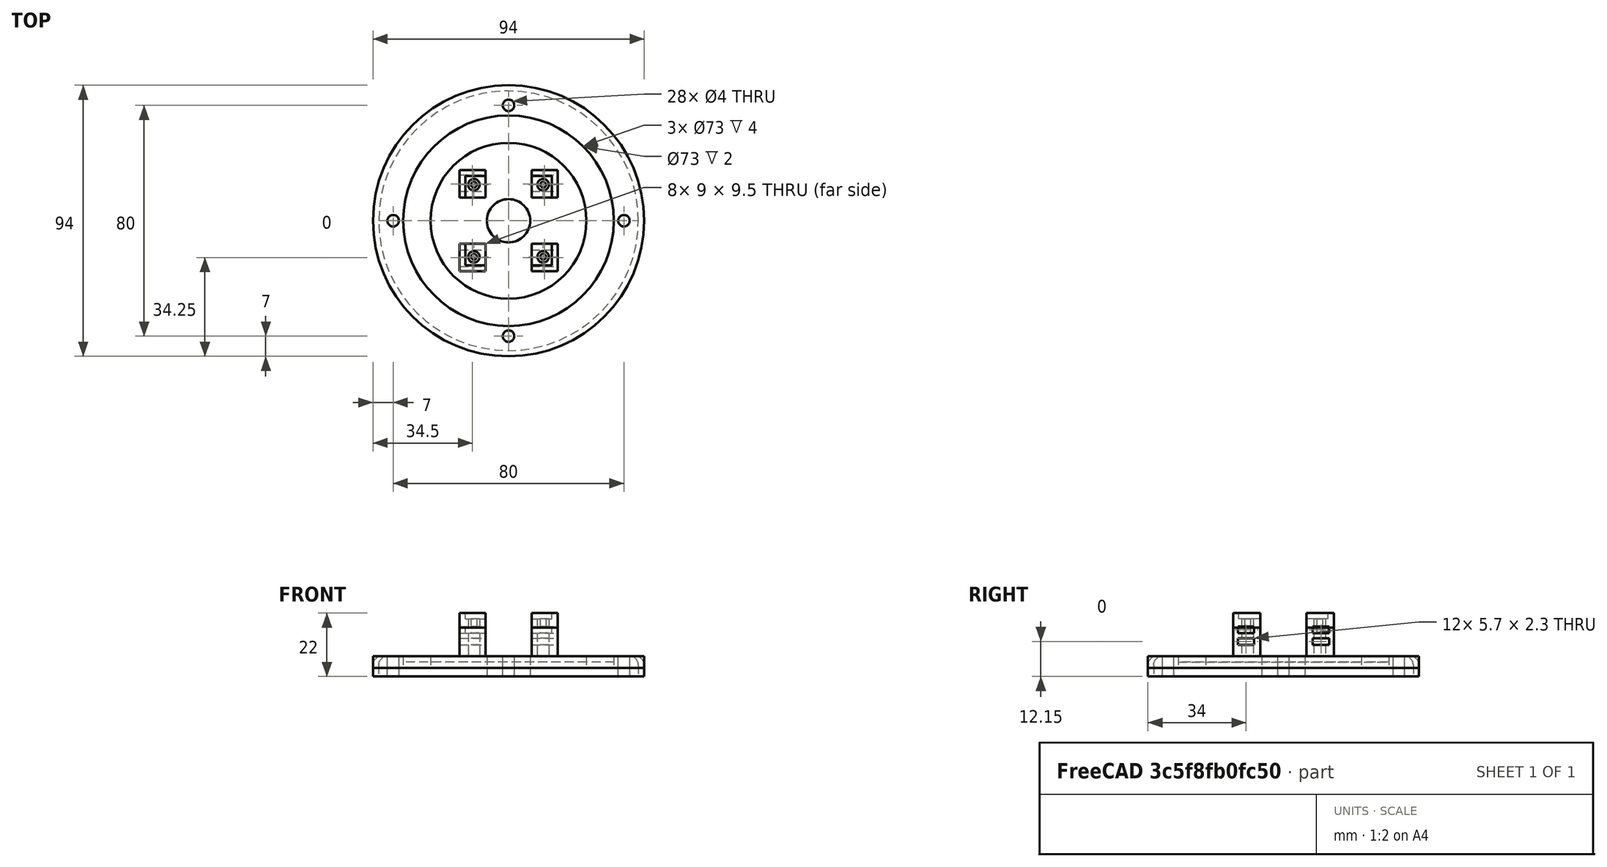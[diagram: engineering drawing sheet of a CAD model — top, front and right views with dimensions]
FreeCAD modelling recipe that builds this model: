
FCSTD DOCUMENT  (FreeCAD 0.16R6700 (Git))
Label: pieza7v1
License: CreativeCommons Attribution-ShareAlike
LicenseURL: http://creativecommons.org/licenses/by-sa/4.0/
objects: Part::Cut×26, Part::Cylinder×16, Part::Feature×12, Part::Box×10, Part::MultiFuse×3, Part::Fillet×2
note: 69 computed .brp shape members not serialized (recipe doc carries the construction recipe); baked Part::Feature solids carry a one-line shape summary decoded from their .brp

FEATURE [Part::Cylinder] Cylinder005  label="Cilindro004"
  Angle = 360
  Height = 5
  Radius = 36.5
FEATURE [Part::Cylinder] Cylinder006  label="Cilindro005"
  Angle = 360
  Height = 8
  Placement = pos=(0,0,-2) rot=(0,0,1;0rad)
  Radius = 27
FEATURE [Part::Cut] Cut016002
  Base = -> Cylinder005
  Placement = pos=(0,0,55) rot=(0,0,1;0rad)
  Tool = -> Cylinder006
FEATURE [Part::Cylinder] Cylinder007  label="prePortaLamH001"
  Angle = 360
  Height = 7
  Placement = pos=(0,0,56) rot=(0,0,1;0rad)
  Radius = 47
FEATURE [Part::Feature] Clone020  label=" taladroTuercaM030"
  Placement = pos=(-1e-11,30,75.05) rot=(1,0,0;3.14159rad)
  shape: bbox 6.7 x 5.802 x 32.25 mm, 10 faces (baked)
FEATURE [Part::Feature] Clone021  label=" taladroTuercaM031"
  Placement = pos=(40,-10,75.05) rot=(1,0,0;3.14159rad)
  shape: bbox 6.7 x 5.802 x 32.25 mm, 10 faces (baked)
FEATURE [Part::Feature] Clone022  label=" taladroTuercaM032"
  Placement = pos=(-1e-11,-50,75.05) rot=(1,0,0;3.14159rad)
  shape: bbox 6.7 x 5.802 x 32.25 mm, 10 faces (baked)
FEATURE [Part::Feature] Clone023  label=" taladroTuercaM033"
  Placement = pos=(-40,-10,75.05) rot=(1,0,0;3.14159rad)
  shape: bbox 6.7 x 5.802 x 32.25 mm, 10 faces (baked)
FEATURE [Part::Cut] Cut016015
  Base = -> Cylinder007
  Tool = -> Cut016002
FEATURE [Part::Cut] Cut016016
  Base = -> Cut016015
  Tool = -> Clone020
FEATURE [Part::Cut] Cut016017
  Base = -> Cut016016
  Tool = -> Clone021
FEATURE [Part::Cut] Cut016018
  Base = -> Cut016017
  Tool = -> Clone022
FEATURE [Part::Cut] Cut016019  label="prePortaCamV2"
  Base = -> Cut016018
  Tool = -> Clone023
FEATURE [Part::Cylinder] Cylinder008  label="Cilindro006"
  Angle = 360
  Height = 25
  Placement = pos=(0,0,43) rot=(0,0,1;0rad)
  Radius = 7.5
FEATURE [Part::Cut] Cut016020
  Base = -> Cut016019
  Tool = -> Cylinder008
FEATURE [Part::Box] Box015  label="Cubo015"
  Height = 2
  Length = 30
  Placement = pos=(-15,-15.5,41) rot=(0,0,1;0rad)
  Width = 31
FEATURE [Part::Cylinder] Cylinder010  label="Cilindro009"
  Angle = 360
  Height = 19
  Placement = pos=(-12,12.5,38) rot=(0,0,1;0rad)
  Radius = 1
FEATURE [Part::Cylinder] Cylinder013  label="Cilindro012"
  Angle = 360
  Height = 19
  Placement = pos=(-12,-12.5,38) rot=(0,0,1;0rad)
  Radius = 1
FEATURE [Part::Cylinder] Cylinder014  label="Cilindro013"
  Angle = 360
  Height = 19
  Placement = pos=(12,-12.5,38) rot=(0,0,1;0rad)
  Radius = 1
FEATURE [Part::Cylinder] Cylinder015  label="Cilindro014"
  Angle = 360
  Height = 19
  Placement = pos=(12,12.5,38) rot=(0,0,1;0rad)
  Radius = 1
FEATURE [Part::Box] Box016  label="Cubo016"
  Height = 16
  Length = 34
  Placement = pos=(-17,-17.5,41) rot=(0,0,1;0rad)
  Width = 35
FEATURE [Part::Box] Box017  label="Cubo017"
  Height = 21
  Length = 49
  Placement = pos=(-25,-8,37) rot=(0,0,1;0rad)
  Width = 16
FEATURE [Part::Box] Box018  label="Cubo018"
  Height = 21
  Length = 49
  Placement = pos=(8,-25,38) rot=(0,0,1;1.5708rad)
  Width = 16
FEATURE [Part::Cut] Cut016021
  Base = -> Box016
  Tool = -> Box017
FEATURE [Part::Cut] Cut016022
  Base = -> Cut016021
  Tool = -> Box018
FEATURE [Part::Cut] Cut016023
  Base = -> Cut016022
  Tool = -> Box015
FEATURE [Part::MultiFuse] Fusion006
  Placement = pos=(0,0,5) rot=(0,0,1;0rad)
  Shapes = -> [Cut016023,Cylinder010,Cylinder013,Cylinder014,Cylinder015]
FEATURE [Part::MultiFuse] Fusion007  label="prePortaCamara"
  Placement = pos=(0,0,0) rot=(1,0,0;3.14159rad)
  Shapes = -> [Cut016020,Fusion006]
FEATURE [Part::Box] Box004  label="Cubo004"
  Height = 2.3
  Length = 80
  Placement = pos=(-40,10.15,-52) rot=(0,0,1;0rad)
  Width = 5.7
FEATURE [Part::Box] Box019  label="Cubo019"
  Height = 2.3
  Length = 80
  Placement = pos=(-40,-15.85,-52) rot=(0,0,1;0rad)
  Width = 5.7
FEATURE [Part::Cylinder] Cylinder016  label="Cilindro015"
  Angle = 360
  Height = 5
  Radius = 36.5
FEATURE [Part::Cylinder] Cylinder017  label="Cilindro016"
  Angle = 360
  Height = 8
  Placement = pos=(0,0,-2) rot=(0,0,1;0rad)
  Radius = 27
FEATURE [Part::Cut] Cut016024
  Base = -> Cylinder016
  Placement = pos=(0,0,55) rot=(0,0,1;0rad)
  Tool = -> Cylinder017
FEATURE [Part::Cylinder] Cylinder018  label="prePortaLamH002"
  Angle = 360
  Height = 7
  Placement = pos=(0,0,56) rot=(0,0,1;0rad)
  Radius = 45
FEATURE [Part::Feature] Clone024  label=" taladroTuercaM034"
  Placement = pos=(-1e-11,30,75.05) rot=(1,0,0;3.14159rad)
  shape: bbox 6.7 x 5.802 x 32.25 mm, 10 faces (baked)
FEATURE [Part::Feature] Clone025  label=" taladroTuercaM035"
  Placement = pos=(40,-10,75.05) rot=(1,0,0;3.14159rad)
  shape: bbox 6.7 x 5.802 x 32.25 mm, 10 faces (baked)
FEATURE [Part::Feature] Clone026  label=" taladroTuercaM036"
  Placement = pos=(-1e-11,-50,75.05) rot=(1,0,0;3.14159rad)
  shape: bbox 6.7 x 5.802 x 32.25 mm, 10 faces (baked)
FEATURE [Part::Feature] Clone027  label=" taladroTuercaM037"
  Placement = pos=(-40,-10,75.05) rot=(1,0,0;3.14159rad)
  shape: bbox 6.7 x 5.802 x 32.25 mm, 10 faces (baked)
FEATURE [Part::Cut] Cut016025
  Base = -> Cylinder018
  Tool = -> Cut016024
FEATURE [Part::Cut] Cut016026
  Base = -> Cut016025
  Tool = -> Clone024
FEATURE [Part::Cut] Cut016027
  Base = -> Cut016026
  Tool = -> Clone025
FEATURE [Part::Cut] Cut016028
  Base = -> Cut016027
  Tool = -> Clone026
FEATURE [Part::Cut] Cut016029  label="prePortaCamV003"
  Base = -> Cut016028
  Tool = -> Clone027
FEATURE [Part::Cylinder] Cylinder019  label="Cilindro017"
  Angle = 360
  Height = 25
  Placement = pos=(0,0,43) rot=(0,0,1;0rad)
  Radius = 7.5
FEATURE [Part::Cut] Cut016030
  Base = -> Cut016029
  Tool = -> Cylinder019
FEATURE [Part::Box] Box020  label="Cubo020"
  Height = 2
  Length = 30
  Placement = pos=(-15,-15.5,41) rot=(0,0,1;0rad)
  Width = 31
FEATURE [Part::Cylinder] Cylinder020  label="Cilindro018"
  Angle = 360
  Height = 19
  Placement = pos=(-12,12.5,38) rot=(0,0,1;0rad)
  Radius = 2
FEATURE [Part::Cylinder] Cylinder021  label="Cilindro019"
  Angle = 360
  Height = 19
  Placement = pos=(-12,-12.5,38) rot=(0,0,1;0rad)
  Radius = 2
FEATURE [Part::Cylinder] Cylinder022  label="Cilindro020"
  Angle = 360
  Height = 19
  Placement = pos=(12,-12.5,38) rot=(0,0,1;0rad)
  Radius = 2
FEATURE [Part::Cylinder] Cylinder023  label="Cilindro021"
  Angle = 360
  Height = 19
  Placement = pos=(12,12.5,38) rot=(0,0,1;0rad)
  Radius = 2
FEATURE [Part::Box] Box021  label="Cubo021"
  Height = 16
  Length = 34
  Placement = pos=(-17,-17.5,41) rot=(0,0,1;0rad)
  Width = 35
FEATURE [Part::Box] Box022  label="Cubo022"
  Height = 21
  Length = 49
  Placement = pos=(-25,-8,37) rot=(0,0,1;0rad)
  Width = 16
FEATURE [Part::Box] Box023  label="Cubo023"
  Height = 21
  Length = 49
  Placement = pos=(8,-25,38) rot=(0,0,1;1.5708rad)
  Width = 16
FEATURE [Part::Cut] Cut016031
  Base = -> Box021
  Tool = -> Box022
FEATURE [Part::Cut] Cut016032
  Base = -> Cut016031
  Tool = -> Box023
FEATURE [Part::Cut] Cut016033
  Base = -> Cut016032
  Tool = -> Box020
FEATURE [Part::Cut] Cut
  Base = -> Cut016033
  Tool = -> Cylinder020
FEATURE [Part::Cut] Cut016034
  Base = -> Cut
  Tool = -> Cylinder021
FEATURE [Part::Cut] Cut016035
  Base = -> Cut016034
  Tool = -> Cylinder022
FEATURE [Part::Cut] Cut016036
  Base = -> Cut016035
  Placement = pos=(0,0,5) rot=(0,0,1;0rad)
  Tool = -> Cylinder023
FEATURE [Part::MultiFuse] Fusion
  Placement = pos=(0,0,0) rot=(1,0,0;3.14159rad)
  Shapes = -> [Cut016030,Cut016036]
FEATURE [Part::Cut] Cut016037
  Base = -> Fusion
  Tool = -> Box004
FEATURE [Part::Feature] Cut016038001  label="csPrePortaCamaraV2"
  shape: bbox 94 x 94 x 19 mm, 72 faces (baked)
FEATURE [Part::Fillet] Fillet  label="prePortaCamaraV1"
  Base = -> Fusion007
  Edges = 1 edges r=3: [Edge3]
FEATURE [Part::Feature] Fillet001  label="csPrePortaCamaraV1"
  shape: bbox 101.7 x 101.7 x 20 mm, 53 faces (baked)
FEATURE [Part::Cut] Cut016038002
  Base = -> Cut016037
  Tool = -> Box019
FEATURE [Part::Fillet] Fillet002  label="prePortaCamaraV2"
  Base = -> Cut016038002
  Edges = 1 edges r=3: [Edge3]
FEATURE [Part::Feature] Fillet002001  label="prePortaCamaraV003"
  shape: bbox 101.7 x 101.7 x 17 mm, 73 faces (baked)
FEATURE [Part::Feature] Fillet002002  label="csPortaCamara45"
  shape: bbox 97.42 x 97.42 x 17 mm, 73 faces (baked)
